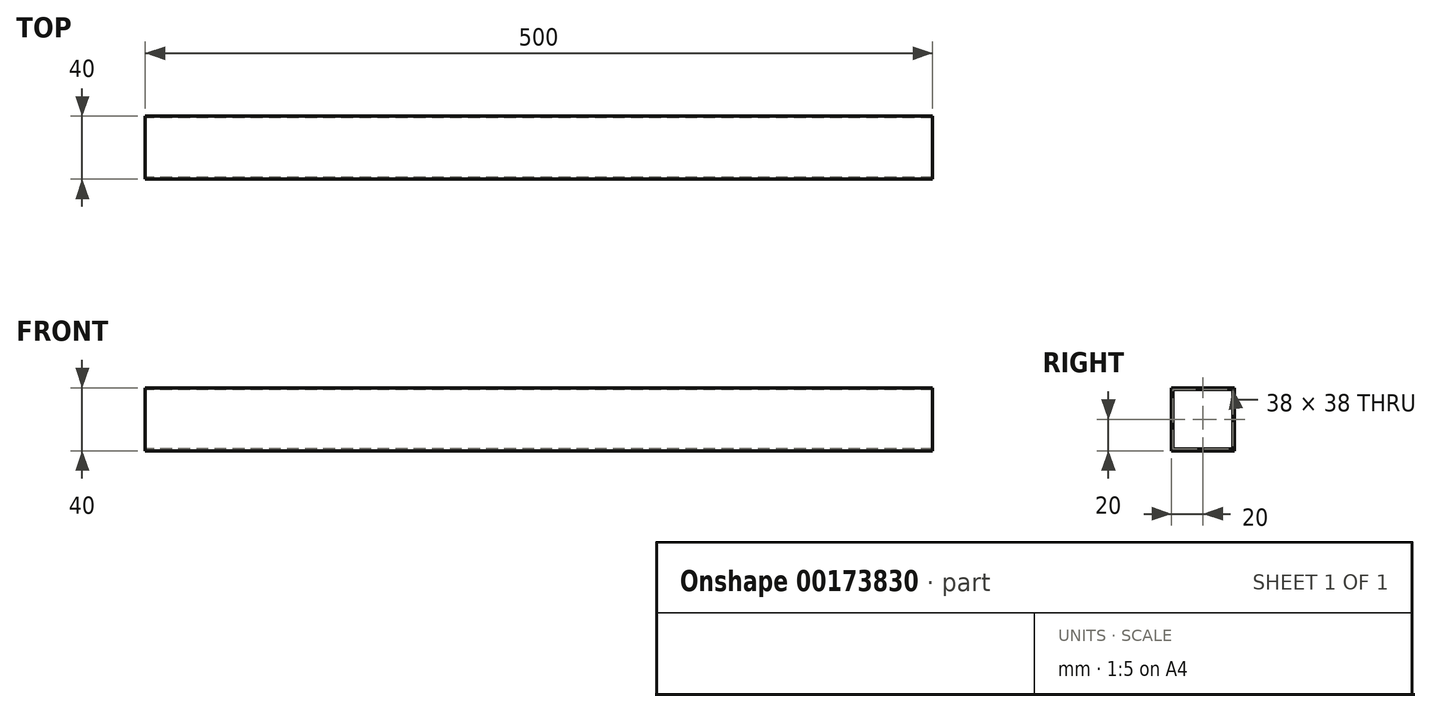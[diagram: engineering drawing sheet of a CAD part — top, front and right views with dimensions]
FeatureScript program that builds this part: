
annotation { "Feature Type Name" : "Feature", "Feature Type Description" : "" }
export const myFeature = defineFeature(function(context is Context, id is Id, definition is map)
    precondition{}
    {
        {
            var Q0;
            Q0=qCreatedBy(makeId("Right.planeOp"),FACE);
            var sketch = newSketch(context, id + "F0", { "sketchPlane" : qUnion([Q0])});
            skLineSegment(sketch, "E0.bottom", {"start": v(0, 0) * mm, "end": v(40, 0) * mm});
            skLineSegment(sketch, "E0.top", {"start": v(0, 40) * mm, "end": v(40, 40) * mm});
            skLineSegment(sketch, "E0.left", {"start": v(0, 0) * mm, "end": v(0, 40) * mm});
            skLineSegment(sketch, "E0.right", {"start": v(40, 0) * mm, "end": v(40, 40) * mm});
            skLineSegment(sketch, "E1.bottom", {"start": v(1, 1) * mm, "end": v(39, 1) * mm});
            skLineSegment(sketch, "E1.top", {"start": v(1, 39) * mm, "end": v(39, 39) * mm});
            skLineSegment(sketch, "E1.left", {"start": v(1, 1) * mm, "end": v(1, 39) * mm});
            skLineSegment(sketch, "E1.right", {"start": v(39, 1) * mm, "end": v(39, 39) * mm});
            skSolve(sketch);
        }
        {
            var Q0;
            Q0=makeQuery(id+"F0.imprint","IMPRINT",FACE,{"disambiguationData":[TD([[makeQuery(id+"F0.imprint","IMPRINT",EDGE,{"derivedFrom":sQuery(id+"F0.wireOp",EDGE,"E0.bottom")}),1.0]])]});
            extrude(context, id + "F1", {"entities" : qUnion([Q0]), "depth" : 500 * mm});
        }
    });
